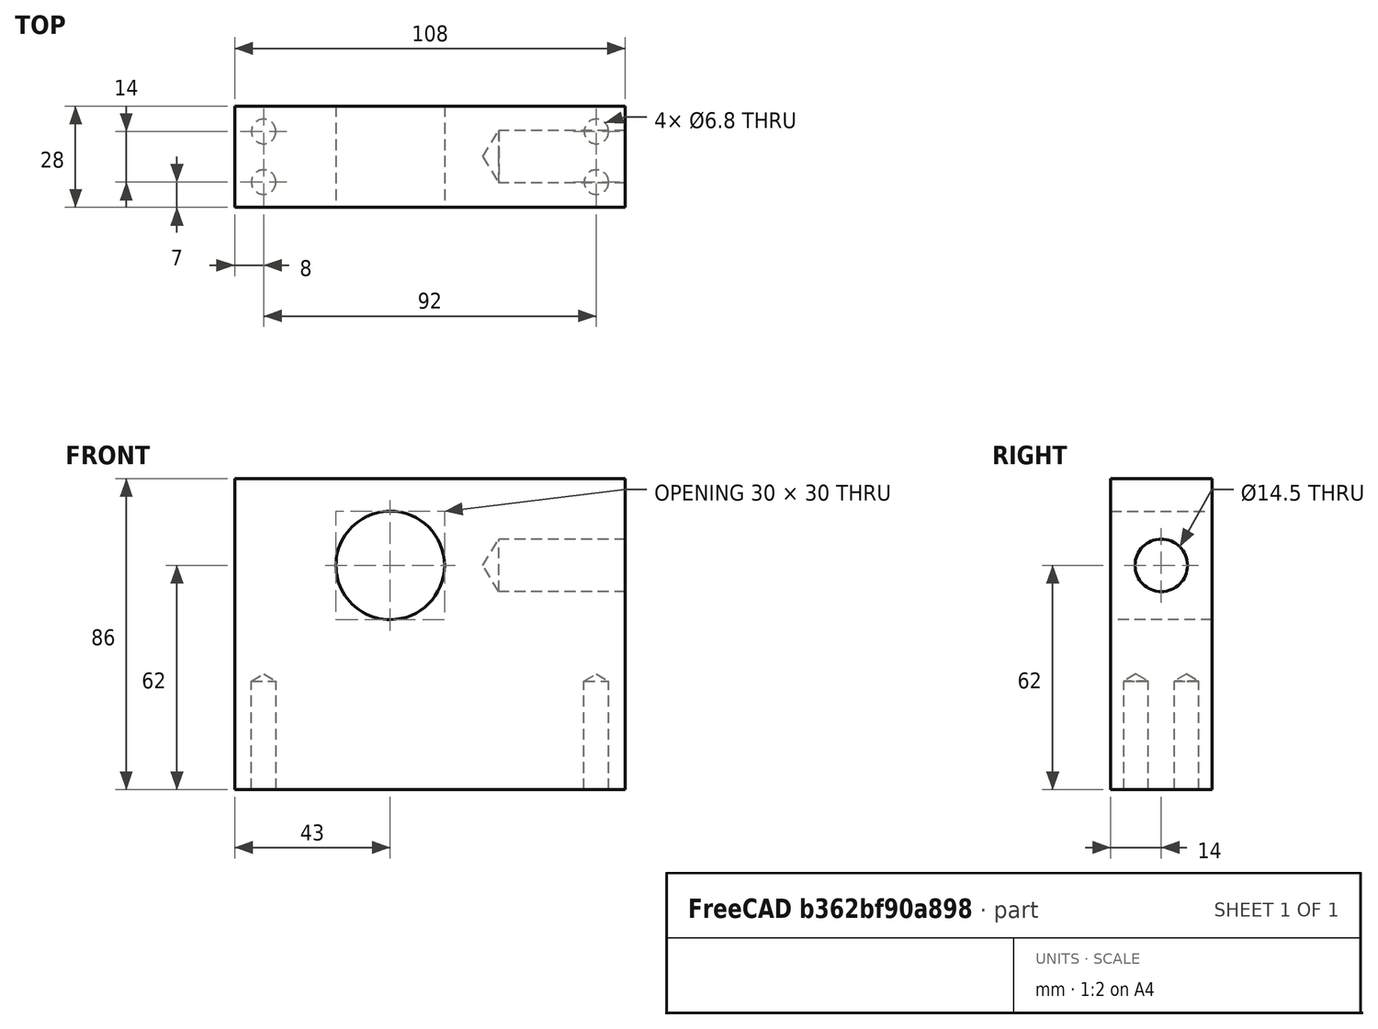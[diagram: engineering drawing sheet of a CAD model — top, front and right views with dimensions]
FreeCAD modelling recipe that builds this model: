
FCSTD DOCUMENT  (FreeCAD 0.19R24267 +99 (Git))
Label: V2 Lever coupling block FEA_CLEARED
License: All rights reserved
LicenseURL: http://en.wikipedia.org/wiki/All_rights_reserved
objects: TechDraw::DrawViewDimension×7, Sketcher::SketchObject×4, TechDraw::DrawViewPart×4, TechDraw::DrawViewBalloon×3, TechDraw::DrawViewAnnotation×3, PartDesign::Hole×2, Fem::ConstraintForce×2, PartDesign::Pad×1, PartDesign::Pocket×1, PartDesign::Body×1, TechDraw::DrawSVGTemplate×1, TechDraw::DrawViewImage×1, TechDraw::DrawPage×1, Fem::FemSolverObjectPython×1, App::MaterialObjectPython×1, Fem::FeaturePython×1, Fem::FemMeshObjectPython×1, Fem::ConstraintFixed×1, Fem::FemAnalysis×1
note: 13 computed .brp shape members not serialized (recipe doc carries the construction recipe); baked Part::Feature solids carry a one-line shape summary decoded from their .brp

FEATURE [Sketcher::SketchObject] Sketch  label="Bottom profile"
  FullyConstrained = true
  MapMode = 5
  Support = -> [XY_Plane]
  sketch-geometry (4):
    g0: LineSegment StartX=-108 StartY=14 StartZ=0 EndX=0 EndY=14 EndZ=0
    g1: LineSegment StartX=0 StartY=14 StartZ=0 EndX=0 EndY=-14 EndZ=0
    g2: LineSegment StartX=0 StartY=-14 StartZ=0 EndX=-108 EndY=-14 EndZ=0
    g3: LineSegment StartX=-108 StartY=-14 StartZ=0 EndX=-108 EndY=14 EndZ=0
  constraints (11):
    c: Coincident(g0,g1)
    c: Coincident(g1,g2)
    c: Coincident(g2,g3)
    c: Coincident(g3,g0)
    c: Horizontal(g0)
    c: Horizontal(g2)
    c: Vertical(g3)
    c: Symmetric(g0,g1,g-1)
    c: DistanceY(g1,g1) = 28
    c: DistanceX(g0,g0) = 108
    c: PointOnObject(g-1,g1)
FEATURE [PartDesign::Pad] Pad  label="Block height"
  Direction = (1,1,1)
  Length = 86
  Length2 = 100
  Profile = -> Sketch
  Type = 0
FEATURE [Sketcher::SketchObject] Sketch001  label="M16 thread hole sketch"
  FullyConstrained = true
  MapMode = 5
  Placement = pos=(0,0,0) rot=(0.57735,0.57735,0.57735;2.0944rad)
  Support = -> [YZ_Plane]
  sketch-geometry (1):
    g0: Circle CenterX=0 CenterY=62 CenterZ=0 NormalX=0 NormalY=0 NormalZ=1 AngleXU=0 Radius=8
  constraints (3):
    c: PointOnObject(g0,g-2)
    c: Radius(g0) = 8
    c: DistanceY(g-1,g0) = 62
FEATURE [Sketcher::SketchObject] Sketch002  label="Lever pin hole sketch"
  FullyConstrained = true
  MapMode = 5
  Placement = pos=(0,0,0) rot=(1,0,0;1.5708rad)
  Support = -> [XZ_Plane]
  sketch-geometry (6):
    g0: GeomPoint X=0 Y=-8 Z=0
    g1: GeomPoint X=0 Y=-38 Z=0
    g2: LineSegment StartX=-65 StartY=62 StartZ=0 EndX=-65 EndY=77 EndZ=0
    g3: LineSegment StartX=-65 StartY=62 StartZ=0 EndX=-64.996 EndY=47 EndZ=0
    g4: ArcOfCircle CenterX=-65 CenterY=62 CenterZ=0 NormalX=0 NormalY=0 NormalZ=1 AngleXU=0 Radius=15 StartAngle=4.71266 EndAngle=7.85398
    g5: ArcOfCircle CenterX=-65 CenterY=62 CenterZ=0 NormalX=0 NormalY=0 NormalZ=1 AngleXU=0 Radius=15 StartAngle=1.5708 EndAngle=4.71266
  constraints (16):
    c: PointOnObject(g0,g-2)
    c: PointOnObject(g1,g-2)
    c: DistanceY(g0,g-1) = 8
    c: DistanceY(g1,g0) = 30
    c: Vertical(g2)
    c: Coincident(g3,g2)
    c: DistanceY(g3,g2) = 30
    c: DistanceY(g1,g2) = 100
    c: Coincident(g4,g2)
    c: Coincident(g4,g2)
    c: Coincident(g4,g3)
    c: Coincident(g5,g2)
    c: Coincident(g5,g3)
    c: Coincident(g5,g2)
    c: DistanceX(g2,g-1) = 65
    c: DistanceY(g-1,g4) = 62
FEATURE [PartDesign::Pocket] Pocket001  label="Lever pin hole"
  BaseFeature = -> Pad
  Length = 5
  Length2 = 100
  Midplane = true
  Profile = -> Sketch002
  Type = 1
FEATURE [Sketcher::SketchObject] Sketch003  label="M8 Bolt hole sketch"
  ExternalGeometry = -> [Pocket001]
  FullyConstrained = true
  MapMode = 5
  Support = -> [XY_Plane]
  sketch-geometry (8):
    g0: LineSegment StartX=-100 StartY=7 StartZ=0 EndX=-8 EndY=7 EndZ=0
    g1: LineSegment StartX=-8 StartY=7 StartZ=0 EndX=-8 EndY=-7 EndZ=0
    g2: LineSegment StartX=-8 StartY=-7 StartZ=0 EndX=-100 EndY=-7 EndZ=0
    g3: LineSegment StartX=-100 StartY=-7 StartZ=0 EndX=-100 EndY=7 EndZ=0
    g4: Circle CenterX=-100 CenterY=7 CenterZ=0 NormalX=0 NormalY=0 NormalZ=1 AngleXU=0 Radius=4
    g5: Circle CenterX=-100 CenterY=-7 CenterZ=0 NormalX=0 NormalY=0 NormalZ=1 AngleXU=0 Radius=4
    g6: Circle CenterX=-8 CenterY=7 CenterZ=0 NormalX=0 NormalY=0 NormalZ=1 AngleXU=0 Radius=4
    g7: Circle CenterX=-8 CenterY=-7 CenterZ=0 NormalX=0 NormalY=0 NormalZ=1 AngleXU=0 Radius=4
  constraints (19):
    c: Coincident(g0,g1)
    c: Coincident(g1,g2)
    c: Coincident(g2,g3)
    c: Coincident(g3,g0)
    c: Horizontal(g0)
    c: Horizontal(g2)
    c: Vertical(g3)
    c: Symmetric(g0,g1,g-1)
    c: Coincident(g4,g0)
    c: Coincident(g5,g2)
    c: Coincident(g6,g0)
    c: Coincident(g7,g1)
    c: Equal(g4,g5)
    c: Equal(g5,g7)
    c: Equal(g7,g6)
    c: Radius(g4) = 4
    c: DistanceY(g3,g3) = 14
    c: DistanceX(g-3,g2) = 8
    c: DistanceX(g1,g-1) = 8
FEATURE [PartDesign::Hole] Hole  label="M8 Bottom threaded holes"
  BaseFeature = -> Pocket001
  Depth = 30
  DepthType = 0
  Diameter = 6.8
  DrillForDepth = false
  DrillPoint = 1
  DrillPointAngle = 118
  HoleCutCountersinkAngle = 90
  HoleCutCustomValues = false
  HoleCutDepth = 0
  HoleCutDiameter = 9.1
  HoleCutType = 0
  ModelActualThread = false
  Profile = -> Sketch003
  Reversed = true
  Tapered = false
  TaperedAngle = 90
  ThreadAngle = 60
  ThreadClass = 0
  ThreadCutOffInner = 0.135316
  ThreadCutOffOuter = 0.270633
  ThreadDirection = 0
  ThreadFit = 0
  ThreadPitch = 1.25
  ThreadSize = 16
  ThreadType = 1
  Threaded = true
FEATURE [PartDesign::Hole] Hole001  label="M16 Fine threaded coupling hole"
  BaseFeature = -> Hole
  Depth = 35
  DepthType = 0
  Diameter = 14.5
  DrillForDepth = false
  DrillPoint = 1
  DrillPointAngle = 118
  HoleCutCountersinkAngle = 90
  HoleCutCustomValues = false
  HoleCutDepth = 0
  HoleCutDiameter = 17.6
  HoleCutType = 0
  ModelActualThread = false
  Profile = -> Sketch001
  Tapered = false
  TaperedAngle = 90
  ThreadAngle = 60
  ThreadClass = 0
  ThreadCutOffInner = 0.16238
  ThreadCutOffOuter = 0.32476
  ThreadDirection = 0
  ThreadFit = 0
  ThreadPitch = 1.5
  ThreadSize = 35
  ThreadType = 2
  Threaded = true
FEATURE [PartDesign::Body] Body
  Group = -> [Sketch,Pad,Sketch001,Sketch002,Pocket001,Sketch003,Hole,Hole001]
  Origin = -> Origin
  Tip = -> Hole001
FEATURE [TechDraw::DrawSVGTemplate] Template
  EditableTexts = AUTHOR_NAME=RICHARD HODGKINSON,DN=N/A,DRAWING_TITLE=COUPLING BLOCK,FC-DATE=13/02/2022,FC-REV=V1.0,FC-SC=DNS,FC-SH=1 / 1,FC-SI=A4,+4 more (map truncated)
  Height = 210
  Orientation = 1
  Width = 297
FEATURE [TechDraw::DrawViewPart] View001
  CoarseView = false
  Direction = (1,0,0)
  Focus = 100
  HardHidden = true
  IsoCount = 0
  IsoHidden = false
  IsoVisible = false
  LockPosition = false
  Perspective = false
  Rotation = 0
  Scale = 0.6
  ScaleType = 0
  SeamHidden = false
  SeamVisible = true
  SmoothHidden = false
  SmoothVisible = true
  Source = -> [Body]
  X = 254.727
  XDirection = (0,1,0)
  Y = 107.293
FEATURE [TechDraw::DrawViewPart] View003
  CoarseView = false
  Direction = (0.577,-0.577,0.577)
  Focus = 100
  HardHidden = true
  IsoCount = 0
  IsoHidden = false
  IsoVisible = false
  LockPosition = false
  Perspective = false
  Rotation = 0
  Scale = 0.6
  ScaleType = 0
  SeamHidden = false
  SeamVisible = true
  SmoothHidden = false
  SmoothVisible = true
  Source = -> [Hole001]
  X = 60.4547
  XDirection = (0.707,0.707,0)
  Y = 149.585
FEATURE [TechDraw::DrawViewBalloon] Balloon003
  BubbleShape = 6
  EndType = 0
  EndTypeScale = 1
  KinkLength = 5
  LockPosition = false
  OriginX = -0.238289
  OriginY = 18.6158
  Rotation = 0
  ScaleType = 0
  ShapeScale = 1
  SourceView = -> View001
  Text = M16X1.5 (FINE) DEPTH 35MM (DRILL POINT EXTRA) THREADED AS FAR AS POSSIBLE
  TextWrapLen = 40
  X = -35.8388
  Y = 73.2379
FEATURE [TechDraw::DrawViewAnnotation] Annotation
  Font = osifont
  LineSpace = 80
  LockPosition = false
  MaxWidth = -1
  Rotation = 0
  ScaleType = 0
  Text = THIS PART IS A COUPLING BETWEEN A DRIVE PIN AND A  | PERPENDICULAR THREADED COUPLING SHAFT UNDER HEAVY  | LOAD (~2.5T, ARROWS), MOUNTED ON A SLIDING CARRIAGE. THE 4  | TAPPED HOLES SECURE THE BLOCK TO THE CARRIAGE. AXIS  | PERPENDICULARITY AND COINCIDENCE BETWEEN THE 30MM/M16  | HOLES IS IMPORTANT AS WELL AS AXIS ALIGNMENT RELATIVE  | TO THE BASE OF THE BLOCK WITH RESPECT TO SKEW ERRORS  | AND RESULTANT REACTIONARY FORCES.
  TextSize = 3
  TextStyle = 0
  X = 60.7822
  Y = 29.0275
FEATURE [TechDraw::DrawViewPart] View002
  CoarseView = false
  Direction = (0,0,-1)
  Focus = 100
  HardHidden = true
  IsoCount = 0
  IsoHidden = false
  IsoVisible = false
  LockPosition = false
  Perspective = false
  Rotation = 0
  Scale = 0.6
  ScaleType = 0
  SeamHidden = false
  SeamVisible = true
  SmoothHidden = false
  SmoothVisible = true
  Source = -> [Body]
  X = 173
  XDirection = (1,0,0)
  Y = 72.5895
FEATURE [TechDraw::DrawViewDimension] Dimension002
  Arbitrary = false
  ArbitraryTolerances = false
  EqualTolerance = false
  FormatSpec = %.2f
  FormatSpecOverTolerance = %+.2f
  FormatSpecUnderTolerance = %+.2f
  Inverted = false
  LockPosition = false
  MeasureType = 1
  OverTolerance = 0
  References2D = -> [View002]
  Rotation = 0
  ScaleType = 0
  TheoreticalExact = false
  Type = 2
  UnderTolerance = -0.2
  X = -42.9396
  Y = 23.4604
FEATURE [TechDraw::DrawViewBalloon] Balloon002
  BubbleShape = 6
  EndType = 0
  EndTypeScale = 1
  KinkLength = 5
  LockPosition = false
  OriginX = -46.2078
  OriginY = 6.67852
  Rotation = 0
  ScaleType = 0
  ShapeScale = 1
  SourceView = -> View002
  Text = 4X M8X1.25 DEPTH 30MM (DRILL POINT EXTRA) THREADED AS FAR AS POSSIBLE
  TextWrapLen = 60
  X = 8.62193
  Y = 43.1529
FEATURE [TechDraw::DrawViewDimension] Dimension012
  Arbitrary = false
  ArbitraryTolerances = false
  EqualTolerance = true
  FormatSpec = %.2f
  FormatSpecOverTolerance = %+.2f
  FormatSpecUnderTolerance = %+.2f
  Inverted = false
  LockPosition = false
  MeasureType = 1
  OverTolerance = 0.1
  References2D = -> [View002]
  Rotation = 0
  ScaleType = 0
  TheoreticalExact = false
  Type = 1
  UnderTolerance = -0.1
  X = 13.2097
  Y = 17.0732
FEATURE [TechDraw::DrawViewAnnotation] Annotation001
  Font = osifont
  LineSpace = 80
  LockPosition = false
  MaxWidth = -1
  Rotation = 0
  ScaleType = 0
  Text = TAPPED HOLE GRID TO BE SYMMETRIC  | ON FINAL BLOCK DIMENSIONS
  TextSize = 3
  TextStyle = 0
  X = 171.791
  Y = 56.4523
FEATURE [TechDraw::DrawViewImage] Image
  Height = 100
  ImageFile = E:/Tensile tester project/Post handover 1/Documentation parts V2/CAD Update/Slider assembly - part designs/Coupling block annotated.PNG
  LockPosition = false
  Rotation = 0
  Scale = 0.65
  ScaleType = 2
  Width = 100
  X = 60.3173
  Y = 78.4023
FEATURE [TechDraw::DrawViewAnnotation] Annotation002
  Font = osifont
  LineSpace = 80
  LockPosition = false
  MaxWidth = -1
  Rotation = 0
  ScaleType = 0
  Text = THREADED HOLE TO BE SYMMETRIC | ON END FACE +/-0.3MM AND |  COINCIDENT WITH FINAL AXIS OF  | PIN HOLE +/-0.2MM
  TextSize = 3
  TextStyle = 0
  X = 252.457
  Y = 68.6173
FEATURE [TechDraw::DrawViewPart] View
  CoarseView = false
  Direction = (0,-1,0)
  Focus = 100
  HardHidden = true
  IsoCount = 0
  IsoHidden = false
  IsoVisible = false
  LockPosition = false
  Perspective = false
  Rotation = 0
  Scale = 0.6
  ScaleType = 0
  SeamHidden = false
  SeamVisible = true
  SmoothHidden = false
  SmoothVisible = true
  Source = -> [Body]
  X = 173
  XDirection = (1,0,0)
  Y = 155.474
FEATURE [TechDraw::DrawViewDimension] Dimension003
  Arbitrary = false
  ArbitraryTolerances = false
  EqualTolerance = true
  FormatSpec = %.2f
  FormatSpecOverTolerance = %+.2f
  FormatSpecUnderTolerance = %+.2f
  Inverted = false
  LockPosition = false
  MeasureType = 1
  OverTolerance = 0.2
  References2D = -> [View]
  Rotation = 0
  ScaleType = 0
  TheoreticalExact = false
  Type = 1
  UnderTolerance = -0.2
  X = -50.4244
  Y = -29.5683
FEATURE [TechDraw::DrawViewDimension] Dimension
  Arbitrary = false
  ArbitraryTolerances = false
  EqualTolerance = true
  FormatSpec = %.2f
  FormatSpecOverTolerance = %+.2f
  FormatSpecUnderTolerance = %+.2f
  Inverted = false
  LockPosition = false
  MeasureType = 1
  OverTolerance = 0.2
  References2D = -> [View]
  Rotation = 0
  ScaleType = 0
  TheoreticalExact = false
  Type = 1
  UnderTolerance = -0.2
  X = -0.658583
  Y = -40.0579
FEATURE [TechDraw::DrawViewDimension] Dimension004
  Arbitrary = false
  ArbitraryTolerances = false
  EqualTolerance = true
  FormatSpec = %.2f
  FormatSpecOverTolerance = %+.2f
  FormatSpecUnderTolerance = %+.2f
  Inverted = false
  LockPosition = false
  MeasureType = 1
  OverTolerance = 0.2
  References2D = -> [View]
  Rotation = 0
  ScaleType = 0
  TheoreticalExact = false
  Type = 2
  UnderTolerance = -0.2
  X = -47.0045
  Y = -4.56522
FEATURE [TechDraw::DrawViewDimension] Dimension001
  Arbitrary = false
  ArbitraryTolerances = false
  EqualTolerance = false
  FormatSpec = %.2f
  FormatSpecOverTolerance = %+.2f
  FormatSpecUnderTolerance = %+.2f
  Inverted = false
  LockPosition = false
  MeasureType = 1
  OverTolerance = 0
  References2D = -> [View]
  Rotation = 0
  ScaleType = 0
  TheoreticalExact = false
  Type = 2
  UnderTolerance = -0.2
  X = -62.595
  Y = -1.4862
FEATURE [TechDraw::DrawViewBalloon] Balloon
  BubbleShape = 6
  EndType = 0
  EndTypeScale = 1
  KinkLength = 5
  LockPosition = false
  OriginX = -11.099
  OriginY = 18.9146
  Rotation = 0
  ScaleType = 0
  ShapeScale = 1
  SourceView = -> View
  Text = SLIDING BUT NOT EXCESSIVE CLEARANCE FIT FOR 30MM DIAMETER +0/-0.1 PIN
  TextWrapLen = 50
  X = 123.512
  Y = 34.0929
FEATURE [TechDraw::DrawViewDimension] Dimension013
  Arbitrary = false
  ArbitraryTolerances = false
  EqualTolerance = true
  FormatSpec = %.2f
  FormatSpecOverTolerance = %+.2f
  FormatSpecUnderTolerance = %+.2f
  Inverted = false
  LockPosition = false
  MeasureType = 1
  OverTolerance = 0.1
  References2D = -> [View002]
  Rotation = 0
  ScaleType = 0
  TheoreticalExact = false
  Type = 2
  UnderTolerance = -0.1
  X = -49.2567
  Y = 23.5254
FEATURE [TechDraw::DrawPage] Page
  KeepUpdated = true
  NextBalloonIndex = 13
  ProjectionType = 0
  Template = -> Template
  Views = -> [View,View001,View002,Dimension,Dimension001,Dimension002,Dimension003,Dimension004,View003,Balloon,Balloon002,Balloon003,Annotation,Dimension012,Annotation001,Image,Annotation002,Dimension013]
FEATURE [Fem::FemSolverObjectPython] SolverCcxTools  # FEM object (typed FeaturePython)
  AnalysisType = 0
  BeamShellResultOutput3D = false
  EigenmodeHighLimit = 1000000
  EigenmodeLowLimit = 0
  EigenmodesCount = 10
  GeometricalNonlinearity = 0
  IterationsControlParameterCutb = 0.25,0.5,0.75,0.85,,,1.5,
  IterationsControlParameterIter = 4,8,9,200,10,400,,200,,
  IterationsControlParameterTimeUse = false
  IterationsThermoMechMaximum = 2000
  IterationsUserDefinedIncrementations = false
  IterationsUserDefinedTimeStepLength = false
  MaterialNonlinearity = 0
  MatrixSolverType = 0
  SplitInputWriter = false
  ThermoMechSteadyState = true
  TimeEnd = 1
  TimeInitialStep = 0.01
FEATURE [App::MaterialObjectPython] MaterialSolid  # material (typed FeaturePython)
  Category = 0
  Material = AuthorAndLicense=CalculiX-Steel,CardName=CalculiX-Steel,Density=7900 kg/m^3,Description=Standard steel material for CalculiX sample calculations,+7 more (map truncated)
FEATURE [Fem::FeaturePython] MeshRegion  # FEM object (typed FeaturePython)
  CharacteristicLength = 0.9
  References = -> [Hole001]
FEATURE [Fem::FemMeshObjectPython] FEMMeshGmsh  # FEM object (typed FeaturePython)
  Algorithm2D = 0
  Algorithm3D = 0
  CharacteristicLengthMax = 5
  CharacteristicLengthMin = 0
  CoherenceMesh = true
  ElementDimension = 0
  ElementOrder = 1
  GeometryTolerance = 1e-06
  GroupsOfNodes = false
  HighOrderOptimize = false
  MeshRegionList = -> [MeshRegion]
  OptimizeNetgen = false
  OptimizeStd = true
  Part = -> Hole001
  RecombineAll = false
  SecondOrderLinear = false
FEATURE [Fem::ConstraintFixed] ConstraintFixed
  NormalDirection = (0,0,1)
  Normals = (4) [(0,0,1),(0,0,1),(0,0,1),(0,0,1)]
  Points = (4) [(0,14,0),(0,4.66667,0),(0,-4.66667,0),(0,-14,0)]
  References = -> [Hole001]
FEATURE [Fem::ConstraintForce] ConstraintForce
  DirectionVector = (-1,0,-0.000134095)
  Force = 30000
  NormalDirection = (1,0,0.000134095)
  Points = (16) [(-65,14,77),(-77.9911,14,69.4988),(-77.989,14,54.4977),(-64.996,14,47),(-65,4.66667,77),(-77.9911,4.66667,69.4988),(-77.989,4.66667,54.4977),+9 more]
  References = -> [Hole001]
  Reversed = true
  Scale = 5
FEATURE [Fem::ConstraintForce] ConstraintForce001
  Direction = -> Hole001 [Edge17]
  DirectionVector = (1,0,0)
  Force = 30000
  NormalDirection = (3e-16,-1e-16,-1)
  Points = (16) [(-1.197e-14,1.4e-14,54.75),(-1.36337e-14,6.27868,65.625),(-1.63963e-14,-6.27868,65.625),(-1.197e-14,1.22243e-14,54.75),(-11.6667,1.65667e-14,54.75),+11 more]
  References = -> [Hole001]
  Reversed = true
  Scale = 5
FEATURE [Fem::FemAnalysis] Analysis
  Group = -> [SolverCcxTools,MaterialSolid,FEMMeshGmsh,ConstraintFixed,ConstraintForce,ConstraintForce001]
